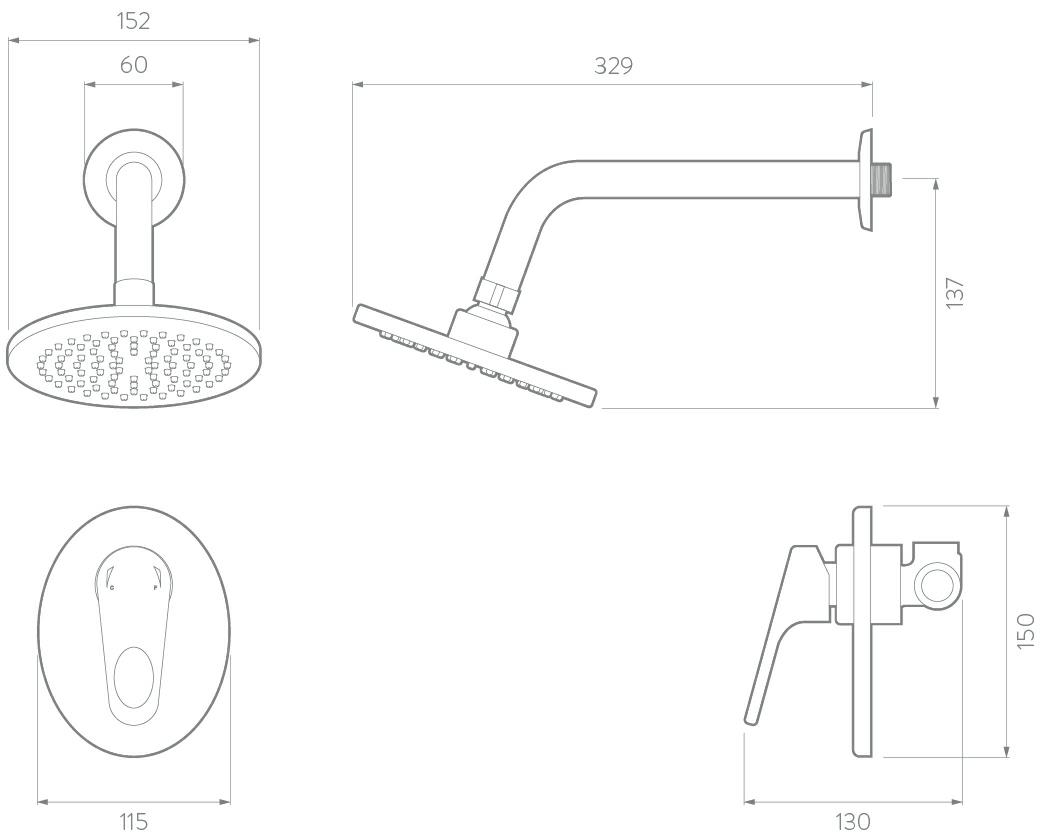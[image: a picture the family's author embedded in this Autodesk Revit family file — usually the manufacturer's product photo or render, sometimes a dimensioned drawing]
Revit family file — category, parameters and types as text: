
# Revit family: DH MONOCONTROL KORAL PRO SSB
name_source: partatom
category: Aparatos sanitarios
revit_build: Autodesk Revit 2018 (Build: 20170223_1515(x64)
units: mm (PartAtom-declared; Revit-internal decimal feet)

## family parameters
Anfitrión = Muro
Compartido = No
Corte con vacíos al cargar = No
Cota de conector redondo = Diámetro de uso
Número OmniClass = 23.45.55.17
Punto de cálculo de habitación = No
Siempre vertical = Sí
Tipo de pieza = Normal
Título OmniClass = Mixing Faucets

## types (1)
- Tipo 1
    Acabado = Brillante
    Altura Nominal = 137
    Ancho Nominal = 152
    Características = Ahorro de agua, mayor cobertura y relajación, idela para espacios medianos, estilo versátil, fácil limpieza, resistente a la corrosión
    Caudal = Promedio 7,9l/min. 80 psi
    Color = Cromo
    Consumo de agua = 9,5l/min.
    Cumplimiento de Norma = Ahorro de agua (9,5l/min.) 80 psi
    Código de montaje = D2010710
    Descripción = Showers
    Descripción IFC = Koral pro sd Ducha Monocontrol
    Descripción de la garantía = Garantía de 30 años por defectos de fabricación, garantía de 3 años en acabados.
    Diámetro de conexión entrada = 1/2 Pulg.
    Duración Garantía Partes = 30
    Duración Garantía Unidad = Años
    Fabricante = www.corona.com.co
    Forma = Regadera Redonda Cuerpo Ovalado
    Información del producto = https://corona.co
    Logitud Nominal = 329
    Material = Cromo-Corona
    Material Secundario = Latón, recubrimiento cromo (acabados)
    Nombre = Ducha Koral
    Nombre del Fabricante = Corona
    Número Modelo = KR4075551
    Presión Máxima = 80 psi.
    Presión Mínima = 20 psi.
    Requerimientos Accesibilidad = Manual
    Responsable Garantías Partes = www.corona.com.co
    Tamaño = 329 x 152 x 137
    Tipo de Activo = Fijo
    Tráfico = Residencial
    Vida útil = 250000 ( Unidad de cierre, Junta Bola )
    Vida útil unidad = Ciclos
